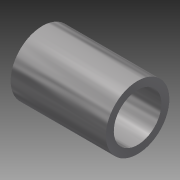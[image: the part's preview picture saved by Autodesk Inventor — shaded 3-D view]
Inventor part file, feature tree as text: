
AUTODESK INVENTOR PART (.ipt)
format: ipt  version: 2015 SP1 (Build 190203100, 203)  size: 104,960 bytes
history: native  units: in
note: dims shown in document units (in); Inventor stores cm internally (conversion verified against a paired STEP export)
features: extrude x1, sketch x1
ambient origin geometry x8: Origin, YZ Plane, XZ Plane, XY Plane, X Axis, Y Axis, Z Axis, Center Point
bodies: Solid1 (feature_tree)
feature tree (2):
  extrude  "Extrusion1"  Depth=0.75in
  sketch  "Sketch1"  dims[d0=0.375in d1=0.5in d2=0.75in d3=0.0in]
